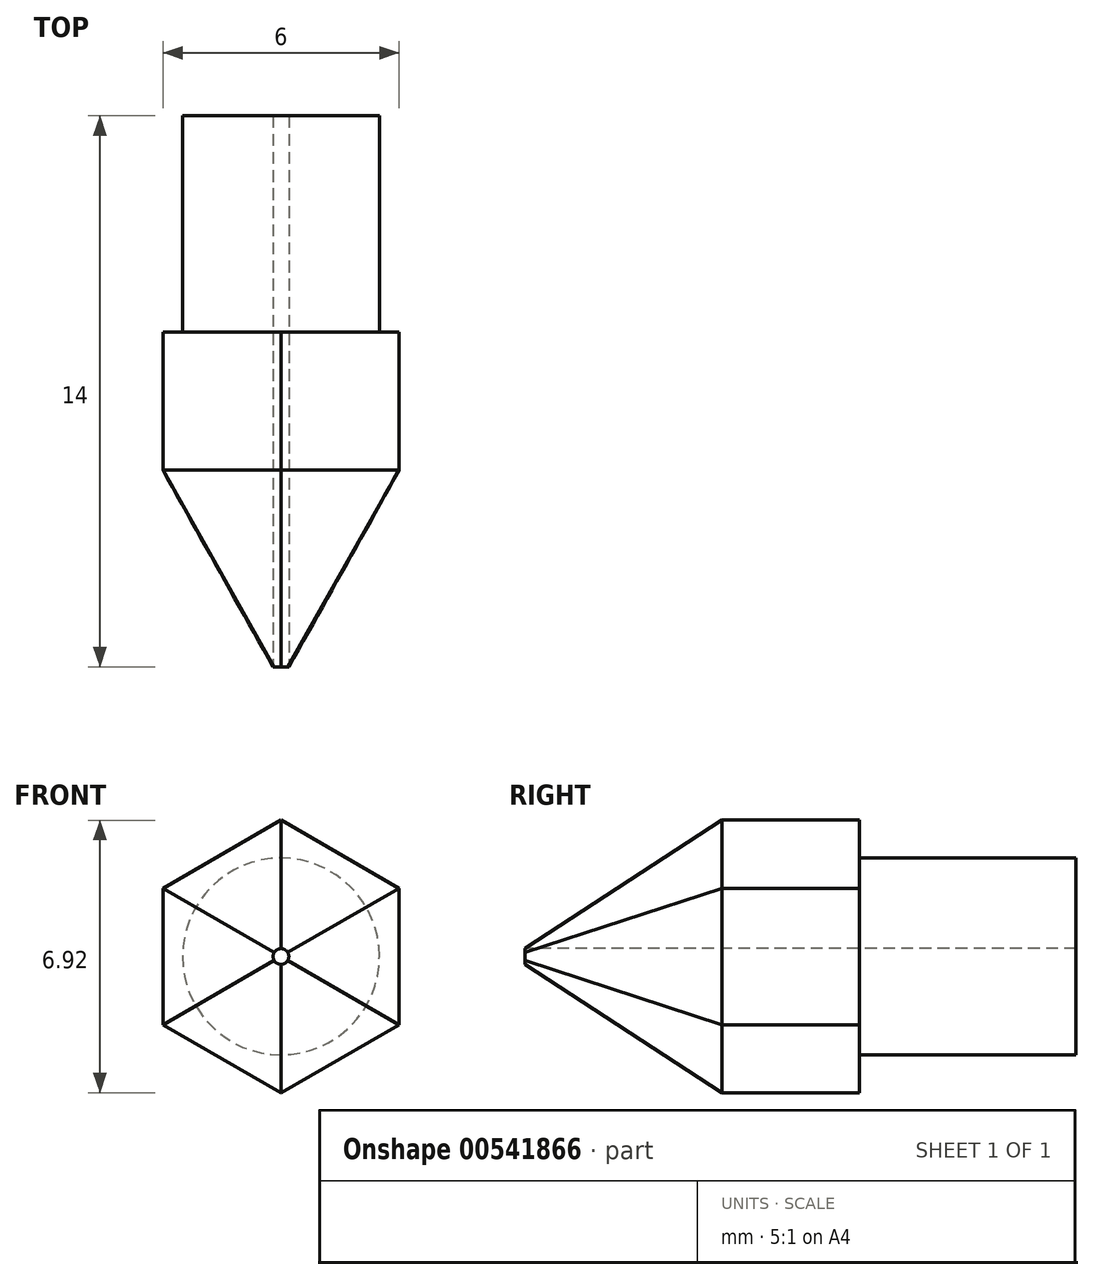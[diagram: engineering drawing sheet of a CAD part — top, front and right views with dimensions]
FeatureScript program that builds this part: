
annotation { "Feature Type Name" : "Feature", "Feature Type Description" : "" }
export const myFeature = defineFeature(function(context is Context, id is Id, definition is map)
    precondition{}
    {
        {
            var Q0;
            Q0=qCreatedBy(makeId("Front.planeOp"),FACE);
            var sketch = newSketch(context, id + "F0", { "sketchPlane" : qUnion([Q0])});
            skCircle(sketch, "E0", {"center": v(0, 0) * mm, "radius": 2.5 * mm});
            skSolve(sketch);
        }
        {
            var Q0;
            Q0=makeQuery(id+"F0.imprint","IMPRINT",FACE,{"disambiguationData":[TD([[makeQuery(id+"F0.imprint","IMPRINT",EDGE,{"derivedFrom":sQuery(id+"F0.wireOp",EDGE,"E0")}),1.0]])]});
            extrude(context, id + "F1", {"entities" : qUnion([Q0]), "depth" : 5.5 * mm, "offsetDistance" : 25 * mm});
        }
        {
            var Q0;
            Q0=makeQuery(id+"F1.opExtrude","CAP_FACE",FACE,{"disambiguationData":[OSD([sQuery(id+"F0.wireOp",EDGE,"E0")])],"isStart":false});
            var sketch = newSketch(context, id + "F2", { "sketchPlane" : qUnion([Q0])});
            skCircle(sketch, "E1.cCircle", {"center": v(0, 0) * mm, "radius": 3 * mm, "construction": true});
            skLineSegment(sketch, "E1.0", {"start": v(3, 1.73) * mm, "end": v(3, -1.73) * mm});
            skLineSegment(sketch, "E1.1", {"start": v(3, -1.73) * mm, "end": v(0, -3.46) * mm});
            skLineSegment(sketch, "E1.2", {"start": v(0, -3.46) * mm, "end": v(-3, -1.73) * mm});
            skLineSegment(sketch, "E1.3", {"start": v(-3, -1.73) * mm, "end": v(-3, 1.73) * mm});
            skLineSegment(sketch, "E1.4", {"start": v(-3, 1.73) * mm, "end": v(0, 3.46) * mm});
            skLineSegment(sketch, "E1.5", {"start": v(0, 3.46) * mm, "end": v(3, 1.73) * mm});
            skPoint(sketch, "E1.0.midPoint", {"position": v(3, 0) * mm});
            skSolve(sketch);
        }
        {
            var Q0;
            Q0=makeQuery(id+"F2.imprint","IMPRINT",FACE,{"disambiguationData":[TD([[makeQuery(id+"F2.imprint","IMPRINT",EDGE,{"derivedFrom":makeQuery(id+"F1.opExtrude","CAP_EDGE",EDGE,{"disambiguationData":[OSD([sQuery(id+"F0.wireOp",EDGE,"E0")])],"isStart":false})}),1.0]])]});
            var Q1;
            Q1=makeQuery(id+"F2.imprint","IMPRINT",FACE,{"disambiguationData":[TD([[makeQuery(id+"F2.imprint","IMPRINT",EDGE,{"derivedFrom":sQuery(id+"F2.wireOp",EDGE,"E1.0")}),-1.0]])]});
            extrude(context, id + "F3", {"entities" : qUnion([Q0, Q1]), "operationType" : NewBodyOperationType.ADD, "depth" : 3.5 * mm, "offsetDistance" : 25 * mm});
        }
        {
            var Q0;
            Q0=makeQuery(id+"F3.opExtrude","CAP_FACE",FACE,{"disambiguationData":[OSD([sQuery(id+"F2.wireOp",EDGE,"E1.0"),sQuery(id+"F2.wireOp",EDGE,"E1.1"),sQuery(id+"F2.wireOp",EDGE,"E1.2"),sQuery(id+"F2.wireOp",EDGE,"E1.3"),sQuery(id+"F2.wireOp",EDGE,"E1.4"),sQuery(id+"F2.wireOp",EDGE,"E1.5")])],"isStart":false});
            cPlane(context, id + "F4", {"entities" : qUnion([Q0]), "cplaneType" : CPlaneType.OFFSET, "offset" : 5 * mm, "width" : 150 * mm, "height" : 150 * mm});
        }
        {
            var Q0;
            Q0=qCreatedBy(id+"F4.planeOp",FACE);
            var sketch = newSketch(context, id + "F5", { "sketchPlane" : qUnion([Q0])});
            skCircle(sketch, "E2", {"center": v(0, 0) * mm, "radius": 0.2 * mm});
            skSolve(sketch);
        }
        {
            var Q1;
            Q1=makeQuery(id+"F5.imprint","IMPRINT",FACE,{"disambiguationData":[TD([[makeQuery(id+"F5.imprint","IMPRINT",EDGE,{"derivedFrom":sQuery(id+"F5.wireOp",EDGE,"E2")}),1.0]])]});
            var Q2;
            Q2=makeQuery(id+"F3.opExtrude","CAP_FACE",FACE,{"disambiguationData":[OSD([sQuery(id+"F2.wireOp",EDGE,"E1.0"),sQuery(id+"F2.wireOp",EDGE,"E1.1"),sQuery(id+"F2.wireOp",EDGE,"E1.2"),sQuery(id+"F2.wireOp",EDGE,"E1.3"),sQuery(id+"F2.wireOp",EDGE,"E1.4"),sQuery(id+"F2.wireOp",EDGE,"E1.5")])],"isStart":false});
            loft(context, id + "F6", {"operationType" : NewBodyOperationType.ADD, "sheetProfilesArray" : [{ "sheetProfileEntities" : qUnion([Q1]) }, { "sheetProfileEntities" : qUnion([Q2]) }]});
        }
        {
            var Q0;
            Q0=makeQuery(id+"F6.opLoft","CAP_FACE",FACE,{"disambiguationData":[OSD([makeQuery(id+"F5.imprint","IMPRINT",FACE,{"disambiguationData":[TD([[makeQuery(id+"F5.imprint","IMPRINT",EDGE,{"derivedFrom":sQuery(id+"F5.wireOp",EDGE,"E2")}),1.0]])]})])],"isStart":true});
            extrude(context, id + "F7", {"entities" : qUnion([Q0]), "operationType" : NewBodyOperationType.REMOVE, "oppositeDirection" : true, "depth" : 25 * mm, "offsetDistance" : 25 * mm});
        }
    });
